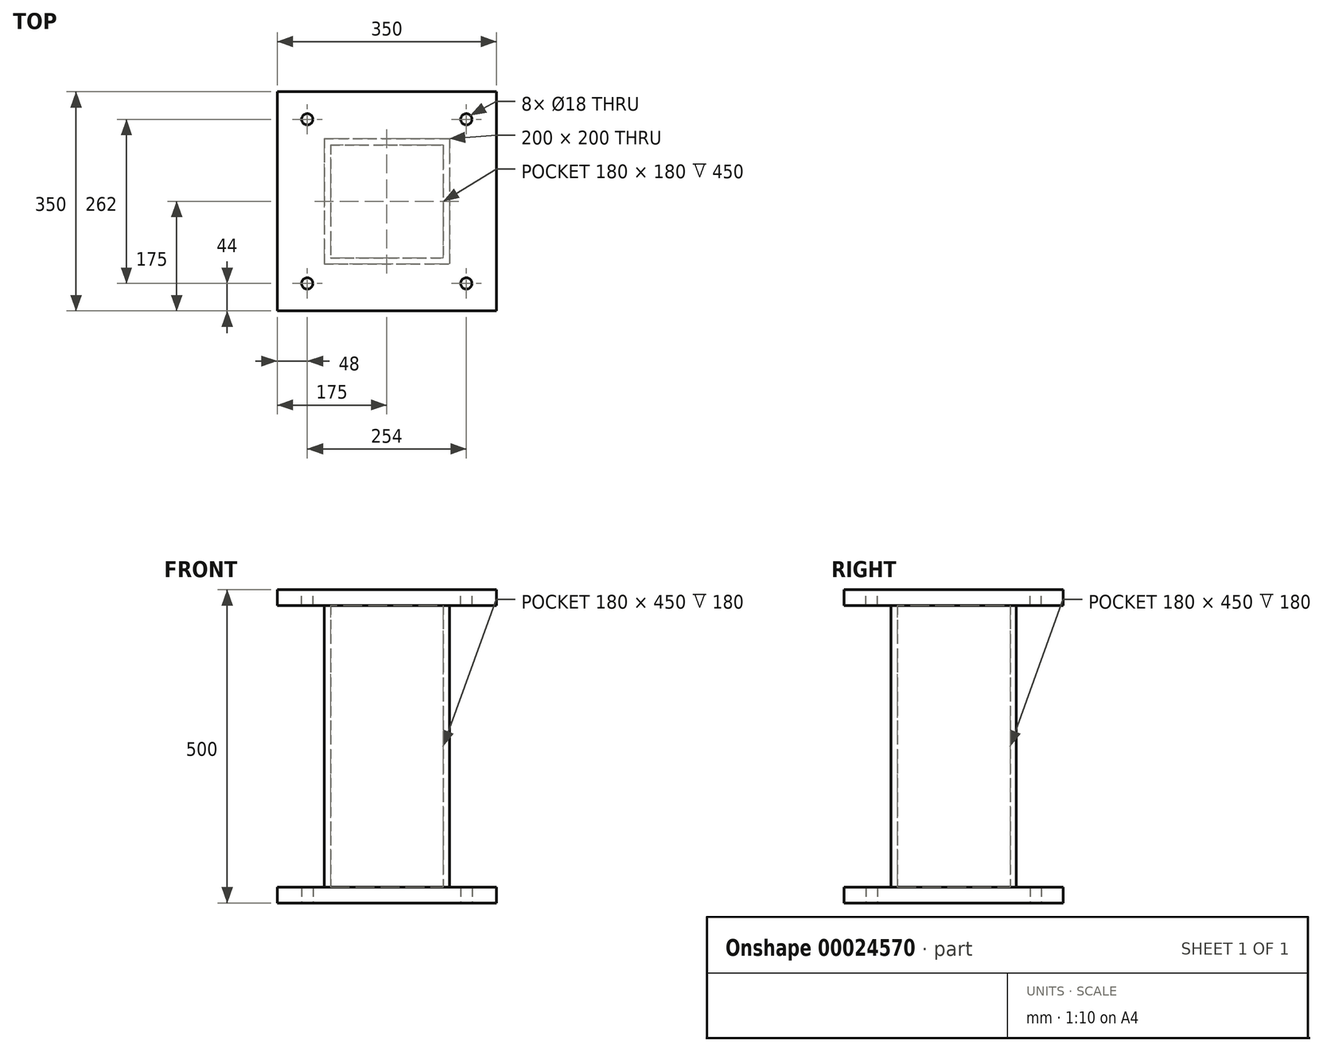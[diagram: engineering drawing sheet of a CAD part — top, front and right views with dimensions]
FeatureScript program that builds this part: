
annotation { "Feature Type Name" : "Feature", "Feature Type Description" : "" }
export const myFeature = defineFeature(function(context is Context, id is Id, definition is map)
    precondition{}
    {
        {
            var Q0;
            Q0=qCreatedBy(makeId("Top.planeOp"),FACE);
            var sketch = newSketch(context, id + "F0", { "sketchPlane" : qUnion([Q0])});
            skLineSegment(sketch, "E0.rect.bottom", {"start": v(175, -175) * mm, "end": v(-175, -175) * mm});
            skLineSegment(sketch, "E0.rect.top", {"start": v(175, 175) * mm, "end": v(-175, 175) * mm});
            skLineSegment(sketch, "E0.rect.left", {"start": v(175, -175) * mm, "end": v(175, 175) * mm});
            skLineSegment(sketch, "E0.rect.right", {"start": v(-175, -175) * mm, "end": v(-175, 175) * mm});
            skPoint(sketch, "E0.rect.middle", {"position": v(0, 0) * mm});
            skCircle(sketch, "E1", {"center": v(-127, 131) * mm, "radius": 9 * mm});
            skCircle(sketch, "E2", {"center": v(127, 131) * mm, "radius": 9 * mm});
            skCircle(sketch, "E3", {"center": v(127, -131) * mm, "radius": 9 * mm});
            skCircle(sketch, "E4", {"center": v(-127, -131) * mm, "radius": 9 * mm});
            skLineSegment(sketch, "E5", {"start": v(127, 131) * mm, "end": v(-127, 131) * mm, "construction": true});
            skLineSegment(sketch, "E6", {"start": v(-127, 131) * mm, "end": v(-127, -131) * mm, "construction": true});
            skLineSegment(sketch, "E7", {"start": v(127, -131) * mm, "end": v(127, 131) * mm, "construction": true});
            skLineSegment(sketch, "E8", {"start": v(127, -131) * mm, "end": v(-127, -131) * mm, "construction": true});
            skSolve(sketch);
        }
        {
            var Q0;
            Q0 = qSketchRegion(id + "F0", true);
            extrude(context, id + "F1", {"entities" : qUnion([Q0]), "depth" : 25 * mm});
        }
        {
            var Q0;
            Q0=makeQuery(id+"F1.opExtrude","CAP_FACE",FACE,{"disambiguationData":[OSD([sQuery(id+"F0.wireOp",EDGE,"E0.rect.bottom"),sQuery(id+"F0.wireOp",EDGE,"E0.rect.top"),sQuery(id+"F0.wireOp",EDGE,"E0.rect.left"),sQuery(id+"F0.wireOp",EDGE,"E0.rect.right"),sQuery(id+"F0.wireOp",EDGE,"E1"),sQuery(id+"F0.wireOp",EDGE,"E2"),sQuery(id+"F0.wireOp",EDGE,"E3"),sQuery(id+"F0.wireOp",EDGE,"E4")])],"isStart":false});
            var sketch = newSketch(context, id + "F2", { "sketchPlane" : qUnion([Q0])});
            skLineSegment(sketch, "E9.rect.bottom", {"start": v(-100, 100) * mm, "end": v(100, 100) * mm});
            skLineSegment(sketch, "E9.rect.top", {"start": v(-100, -100) * mm, "end": v(100, -100) * mm});
            skLineSegment(sketch, "E9.rect.left", {"start": v(-100, 100) * mm, "end": v(-100, -100) * mm});
            skLineSegment(sketch, "E9.rect.right", {"start": v(100, 100) * mm, "end": v(100, -100) * mm});
            skPoint(sketch, "E9.rect.middle", {"position": v(0, 0) * mm});
            skLineSegment(sketch, "E10.rect.bottom", {"start": v(-90, 90) * mm, "end": v(90, 90) * mm});
            skLineSegment(sketch, "E10.rect.top", {"start": v(-90, -90) * mm, "end": v(90, -90) * mm});
            skLineSegment(sketch, "E10.rect.left", {"start": v(-90, 90) * mm, "end": v(-90, -90) * mm});
            skLineSegment(sketch, "E10.rect.right", {"start": v(90, 90) * mm, "end": v(90, -90) * mm});
            skSolve(sketch);
        }
        {
            var Q0;
            Q0 = qSketchRegion(id + "F2", true);
            extrude(context, id + "F3", {"entities" : qUnion([Q0]), "operationType" : NewBodyOperationType.ADD, "depth" : 450 * mm});
        }
        {
            var Q0;
            Q0=makeQuery(id+"F3.opExtrude","SWEPT_EDGE",EDGE,{"disambiguationData":[OSD([sQuery(id+"F2.wireOp",EDGE,"E9.rect.bottom"),sQuery(id+"F2.wireOp",EDGE,"E9.rect.left")])]});
            cPlane(context, id + "F4", {"entities" : qUnion([Q0]), "cplaneType" : CPlaneType.MID_PLANE, "offset" : 150 * mm, "width" : 150 * mm, "height" : 150 * mm});
        }
        {
            var Q0;
            Q0=makeQuery(id+"F1.opExtrude","SWEPT_BODY",BODY,{"disambiguationData":[OSD([sQuery(id+"F0.wireOp",EDGE,"E0.rect.bottom"),sQuery(id+"F0.wireOp",EDGE,"E0.rect.top"),sQuery(id+"F0.wireOp",EDGE,"E0.rect.left"),sQuery(id+"F0.wireOp",EDGE,"E0.rect.right"),sQuery(id+"F0.wireOp",EDGE,"E1"),sQuery(id+"F0.wireOp",EDGE,"E2"),sQuery(id+"F0.wireOp",EDGE,"E3"),sQuery(id+"F0.wireOp",EDGE,"E4")])]});
            var Q1;
            Q1=qCreatedBy(id+"F4.planeOp",FACE);
            mirror(context, id + "F5", {"operationType" : NewBodyOperationType.ADD, "entities" : qUnion([Q0]), "mirrorPlane" : qUnion([Q1])});
        }
    });
